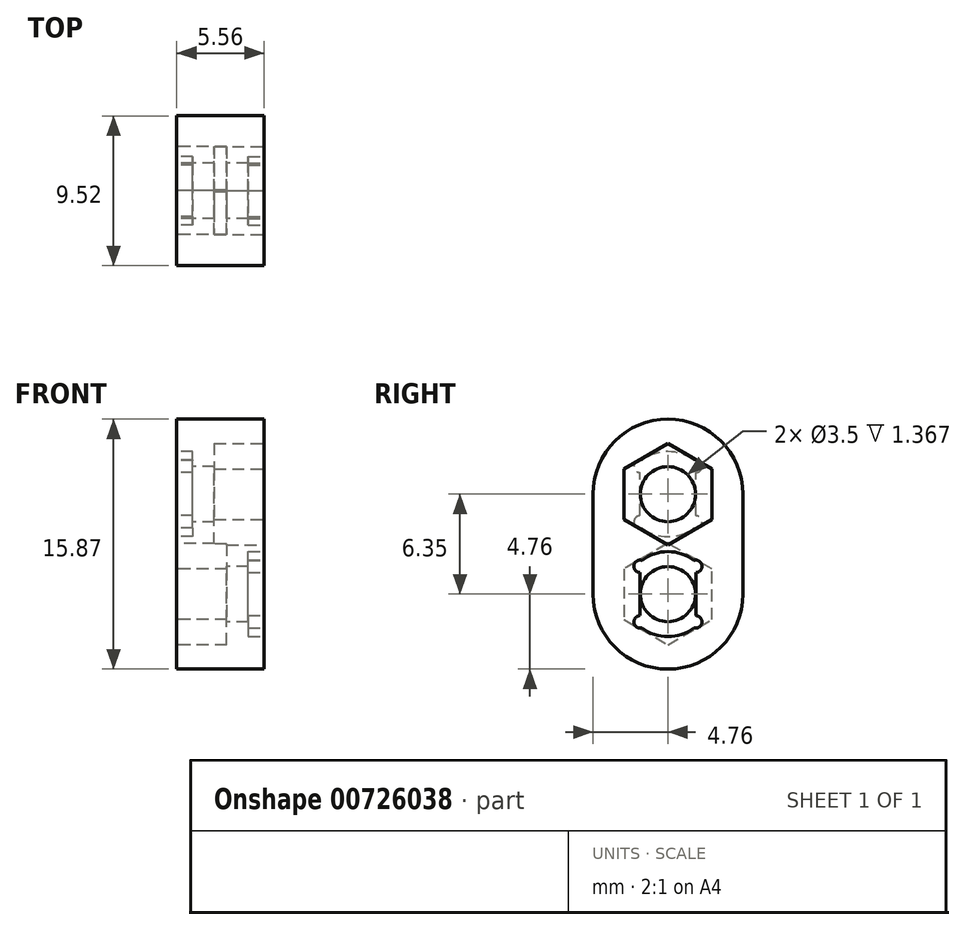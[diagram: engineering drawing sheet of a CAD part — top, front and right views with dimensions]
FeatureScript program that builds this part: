
annotation { "Feature Type Name" : "Feature", "Feature Type Description" : "" }
export const myFeature = defineFeature(function(context is Context, id is Id, definition is map)
    precondition{}
    {
        {
            var Q0;
            Q0=qCreatedBy(makeId("Right.planeOp"),FACE);
            var sketch = newSketch(context, id + "F0", { "sketchPlane" : qUnion([Q0])});
            skCircle(sketch, "E0", {"center": v(0, 0) * mm, "radius": 4.76 * mm});
            skCircle(sketch, "E1", {"center": v(0, 0) * mm, "radius": 1.75 * mm});
            skCircle(sketch, "E2", {"center": v(0, -6.35) * mm, "radius": 4.76 * mm});
            skCircle(sketch, "E3", {"center": v(0, -6.35) * mm, "radius": 1.75 * mm});
            skLineSegment(sketch, "E4", {"start": v(-4.76, 0) * mm, "end": v(-4.76, -6.35) * mm});
            skLineSegment(sketch, "E5", {"start": v(4.76, 0) * mm, "end": v(4.76, -6.35) * mm});
            skSolve(sketch);
        }
        {
            var Q0;
            Q0=makeQuery(id+"F0.imprint","IMPRINT",FACE,{"disambiguationData":[TD([[makeQuery(id+"F0.imprint","IMPRINT",EDGE,{"derivedFrom":sQuery(id+"F0.wireOp",EDGE,"E1")}),-1.0]])]});
            var Q1;
            {var subQ0=sQuery(id+"F0.wireOp",EDGE,"E5");Q1=makeQuery(id+"F0.imprint","IMPRINT",FACE,{"disambiguationData":[TD([[makeQuery(id+"F0.imprint","IMPRINT",EDGE,{"derivedFrom":subQ0}),-1.0]])]});}
            var Q2;
            {var subQ0=sQuery(id+"F0.wireOp",EDGE,"E2");var subQ1=sQuery(id+"F0.wireOp",EDGE,"E0");var subQ2=makeQuery(id+"F0.imprint","INTERSECT",VERTEX,{"disambiguationData":[OD(0.0)],"derivedFrom":[subQ1,subQ0]});Q2=makeQuery(id+"F0.imprint","IMPRINT",FACE,{"disambiguationData":[TD([[makeQuery(id+"F0.imprint","IMPRINT",EDGE,{"disambiguationData":[TD([[subQ2,-1.0]])],"derivedFrom":subQ1}),1.0]])]});}
            var Q3;
            Q3=makeQuery(id+"F0.imprint","IMPRINT",FACE,{"disambiguationData":[TD([[makeQuery(id+"F0.imprint","IMPRINT",EDGE,{"derivedFrom":sQuery(id+"F0.wireOp",EDGE,"E3")}),-1.0]])]});
            var Q4;
            {var subQ0=sQuery(id+"F0.wireOp",EDGE,"E4");Q4=makeQuery(id+"F0.imprint","IMPRINT",FACE,{"disambiguationData":[TD([[makeQuery(id+"F0.imprint","IMPRINT",EDGE,{"derivedFrom":subQ0}),1.0]])]});}
            extrude(context, id + "F1", {"entities" : qUnion([Q0, Q1, Q2, Q3, Q4]), "depth" : 5.56 * mm, "offsetDistance" : 25.4 * mm});
        }
        {
            var Q0;
            Q0=makeQuery(id+"F1.opExtrude","CAP_FACE",FACE,{"disambiguationData":[OSD([sQuery(id+"F0.wireOp",EDGE,"E0"),sQuery(id+"F0.wireOp",EDGE,"E1"),sQuery(id+"F0.wireOp",EDGE,"E2"),sQuery(id+"F0.wireOp",EDGE,"E3"),sQuery(id+"F0.wireOp",EDGE,"E4"),sQuery(id+"F0.wireOp",EDGE,"E5")])],"isStart":false});
            var sketch = newSketch(context, id + "F2", { "sketchPlane" : qUnion([Q0])});
            skLineSegment(sketch, "E6.bottom", {"start": v(-1.77, -8.12) * mm, "end": v(1.77, -8.12) * mm});
            skLineSegment(sketch, "E6.top", {"start": v(-1.77, -4.58) * mm, "end": v(1.77, -4.58) * mm});
            skLineSegment(sketch, "E6.left", {"start": v(-1.77, -8.12) * mm, "end": v(-1.77, -4.58) * mm});
            skLineSegment(sketch, "E6.right", {"start": v(1.77, -8.12) * mm, "end": v(1.77, -4.58) * mm});
            skPoint(sketch, "E6.middle", {"position": v(0, -6.35) * mm});
            skCircle(sketch, "E7", {"center": v(1.77, -4.58) * mm, "radius": 0.4 * mm});
            skCircle(sketch, "E8", {"center": v(-1.77, -4.58) * mm, "radius": 0.4 * mm});
            skCircle(sketch, "E9", {"center": v(-1.77, -8.12) * mm, "radius": 0.4 * mm});
            skCircle(sketch, "E10", {"center": v(1.77, -8.12) * mm, "radius": 0.4 * mm});
            skCircle(sketch, "E11.cCircle", {"center": v(0, 0) * mm, "radius": 3.23 * mm, "construction": true});
            skLineSegment(sketch, "E11.0", {"start": v(0, -3.23) * mm, "end": v(-2.8, -1.61) * mm});
            skLineSegment(sketch, "E11.1", {"start": v(-2.8, -1.61) * mm, "end": v(-2.8, 1.61) * mm});
            skLineSegment(sketch, "E11.2", {"start": v(-2.8, 1.61) * mm, "end": v(0, 3.23) * mm});
            skLineSegment(sketch, "E11.3", {"start": v(0, 3.23) * mm, "end": v(2.8, 1.61) * mm});
            skLineSegment(sketch, "E11.4", {"start": v(2.8, 1.61) * mm, "end": v(2.8, -1.61) * mm});
            skLineSegment(sketch, "E11.5", {"start": v(2.8, -1.61) * mm, "end": v(0, -3.23) * mm});
            skCircle(sketch, "E12", {"center": v(0, -6.35) * mm, "radius": 2.7 * mm});
            skSolve(sketch);
        }
        {
            var Q0;
            {var subQ0=sQuery(id+"F2.wireOp",EDGE,"E6.right");var subQ1=sQuery(id+"F2.wireOp",EDGE,"E6.top");var subQ2=makeQuery(id+"F2.imprint","INTERSECT",VERTEX,{"derivedFrom":[subQ1,subQ0]});Q0=makeQuery(id+"F2.imprint","IMPRINT",FACE,{"disambiguationData":[TD([[makeQuery(id+"F2.imprint","IMPRINT",EDGE,{"disambiguationData":[TD([[subQ2,1.0]])],"derivedFrom":subQ1}),-1.0]])]});}
            var Q1;
            {var subQ0=sQuery(id+"F2.wireOp",EDGE,"E6.right");var subQ1=sQuery(id+"F2.wireOp",EDGE,"E6.top");var subQ2=makeQuery(id+"F2.imprint","INTERSECT",VERTEX,{"derivedFrom":[subQ1,subQ0]});Q1=makeQuery(id+"F2.imprint","IMPRINT",FACE,{"disambiguationData":[TD([[makeQuery(id+"F2.imprint","IMPRINT",EDGE,{"disambiguationData":[TD([[subQ2,1.0]])],"derivedFrom":subQ1}),1.0]])]});}
            var Q2;
            {var subQ0=sQuery(id+"F2.wireOp",EDGE,"E6.right");var subQ1=sQuery(id+"F2.wireOp",EDGE,"E6.bottom");var subQ2=makeQuery(id+"F2.imprint","INTERSECT",VERTEX,{"derivedFrom":[subQ1,subQ0]});Q2=makeQuery(id+"F2.imprint","IMPRINT",FACE,{"disambiguationData":[TD([[makeQuery(id+"F2.imprint","IMPRINT",EDGE,{"disambiguationData":[TD([[subQ2,1.0]])],"derivedFrom":subQ1}),1.0]])]});}
            var Q3;
            {var subQ0=sQuery(id+"F2.wireOp",EDGE,"E6.right");var subQ1=sQuery(id+"F2.wireOp",EDGE,"E6.bottom");var subQ2=makeQuery(id+"F2.imprint","INTERSECT",VERTEX,{"derivedFrom":[subQ1,subQ0]});Q3=makeQuery(id+"F2.imprint","IMPRINT",FACE,{"disambiguationData":[TD([[makeQuery(id+"F2.imprint","IMPRINT",EDGE,{"disambiguationData":[TD([[subQ2,1.0]])],"derivedFrom":subQ1}),-1.0]])]});}
            var Q4;
            {var subQ0=sQuery(id+"F2.wireOp",EDGE,"E6.left");var subQ1=sQuery(id+"F2.wireOp",EDGE,"E6.bottom");var subQ2=makeQuery(id+"F2.imprint","INTERSECT",VERTEX,{"derivedFrom":[subQ1,subQ0]});Q4=makeQuery(id+"F2.imprint","IMPRINT",FACE,{"disambiguationData":[TD([[makeQuery(id+"F2.imprint","IMPRINT",EDGE,{"disambiguationData":[TD([[subQ2,-1.0]])],"derivedFrom":subQ1}),-1.0]])]});}
            var Q5;
            {var subQ0=sQuery(id+"F2.wireOp",EDGE,"E6.left");var subQ1=sQuery(id+"F2.wireOp",EDGE,"E6.bottom");var subQ2=makeQuery(id+"F2.imprint","INTERSECT",VERTEX,{"derivedFrom":[subQ1,subQ0]});Q5=makeQuery(id+"F2.imprint","IMPRINT",FACE,{"disambiguationData":[TD([[makeQuery(id+"F2.imprint","IMPRINT",EDGE,{"disambiguationData":[TD([[subQ2,-1.0]])],"derivedFrom":subQ1}),1.0]])]});}
            var Q6;
            {var subQ0=sQuery(id+"F2.wireOp",EDGE,"E6.left");var subQ1=sQuery(id+"F2.wireOp",EDGE,"E6.top");var subQ2=makeQuery(id+"F2.imprint","INTERSECT",VERTEX,{"derivedFrom":[subQ1,subQ0]});Q6=makeQuery(id+"F2.imprint","IMPRINT",FACE,{"disambiguationData":[TD([[makeQuery(id+"F2.imprint","IMPRINT",EDGE,{"disambiguationData":[TD([[subQ2,-1.0]])],"derivedFrom":subQ1}),-1.0]])]});}
            var Q7;
            {var subQ0=sQuery(id+"F2.wireOp",EDGE,"E6.left");var subQ1=makeQuery(id+"F1.opExtrude","CAP_EDGE",EDGE,{"disambiguationData":[OSD([sQuery(id+"F0.wireOp",EDGE,"E3")])],"isStart":false});var subQ2=makeQuery(id+"F2.imprint","INTERSECT",VERTEX,{"disambiguationData":[OD(0.0)],"derivedFrom":[subQ1,subQ0]});Q7=makeQuery(id+"F2.imprint","IMPRINT",FACE,{"disambiguationData":[TD([[makeQuery(id+"F2.imprint","IMPRINT",EDGE,{"disambiguationData":[TD([[subQ2,-1.0]])],"derivedFrom":subQ0}),-1.0]])]});}
            var Q8;
            {var subQ0=sQuery(id+"F2.wireOp",EDGE,"E6.left");var subQ1=sQuery(id+"F2.wireOp",EDGE,"E6.top");var subQ2=makeQuery(id+"F2.imprint","INTERSECT",VERTEX,{"derivedFrom":[subQ1,subQ0]});Q8=makeQuery(id+"F2.imprint","IMPRINT",FACE,{"disambiguationData":[TD([[makeQuery(id+"F2.imprint","IMPRINT",EDGE,{"disambiguationData":[TD([[subQ2,-1.0]])],"derivedFrom":subQ1}),1.0]])]});}
            var Q9;
            {var subQ1=sQuery(id+"F2.wireOp",EDGE,"E6.top");var subQ7=sQuery(id+"F2.wireOp",EDGE,"E8");var subQ11=makeQuery(id+"F2.imprint","INTERSECT",VERTEX,{"derivedFrom":[subQ1,subQ7]});Q9=makeQuery(id+"F2.imprint","IMPRINT",FACE,{"disambiguationData":[TD([[makeQuery(id+"F2.imprint","IMPRINT",EDGE,{"disambiguationData":[TD([[subQ11,-1.0]])],"derivedFrom":subQ1}),-1.0]])]});}
            var Q10;
            {var subQ0=sQuery(id+"F2.wireOp",EDGE,"E9");var subQ1=sQuery(id+"F2.wireOp",EDGE,"E6.bottom");var subQ2=makeQuery(id+"F2.imprint","INTERSECT",VERTEX,{"derivedFrom":[subQ1,subQ0]});Q10=makeQuery(id+"F2.imprint","IMPRINT",FACE,{"disambiguationData":[TD([[makeQuery(id+"F2.imprint","IMPRINT",EDGE,{"disambiguationData":[TD([[subQ2,-1.0]])],"derivedFrom":subQ1}),1.0]])]});}
            var Q11;
            {var subQ0=sQuery(id+"F2.wireOp",EDGE,"E12");var subQ1=sQuery(id+"F2.wireOp",EDGE,"E6.top");var subQ10=makeQuery(id+"F2.imprint","INTERSECT",VERTEX,{"disambiguationData":[OD(0.0)],"derivedFrom":[subQ1,subQ0]});Q11=makeQuery(id+"F2.imprint","IMPRINT",FACE,{"disambiguationData":[TD([[makeQuery(id+"F2.imprint","IMPRINT",EDGE,{"disambiguationData":[TD([[subQ10,-1.0]])],"derivedFrom":subQ1}),-1.0]])]});}
            var Q12;
            {var subQ0=sQuery(id+"F2.wireOp",EDGE,"E12");var subQ1=sQuery(id+"F2.wireOp",EDGE,"E6.top");var subQ2=makeQuery(id+"F2.imprint","INTERSECT",VERTEX,{"disambiguationData":[OD(1.0)],"derivedFrom":[subQ1,subQ0]});Q12=makeQuery(id+"F2.imprint","IMPRINT",FACE,{"disambiguationData":[TD([[makeQuery(id+"F2.imprint","IMPRINT",EDGE,{"disambiguationData":[TD([[subQ2,-1.0]])],"derivedFrom":subQ1}),-1.0]])]});}
            var Q13;
            {var subQ0=sQuery(id+"F2.wireOp",EDGE,"E12");var subQ1=sQuery(id+"F2.wireOp",EDGE,"E6.top");var subQ2=makeQuery(id+"F2.imprint","INTERSECT",VERTEX,{"disambiguationData":[OD(0.0)],"derivedFrom":[subQ1,subQ0]});Q13=makeQuery(id+"F2.imprint","IMPRINT",FACE,{"disambiguationData":[TD([[makeQuery(id+"F2.imprint","IMPRINT",EDGE,{"disambiguationData":[TD([[subQ2,-1.0]])],"derivedFrom":subQ1}),1.0]])]});}
            var Q14;
            {var subQ0=sQuery(id+"F2.wireOp",EDGE,"E12");var subQ7=sQuery(id+"F2.wireOp",EDGE,"E6.bottom");var subQ8=makeQuery(id+"F2.imprint","INTERSECT",VERTEX,{"disambiguationData":[OD(0.0)],"derivedFrom":[subQ7,subQ0]});Q14=makeQuery(id+"F2.imprint","IMPRINT",FACE,{"disambiguationData":[TD([[makeQuery(id+"F2.imprint","IMPRINT",EDGE,{"disambiguationData":[TD([[subQ8,-1.0]])],"derivedFrom":subQ7}),1.0]])]});}
            var Q15;
            {var subQ0=sQuery(id+"F2.wireOp",EDGE,"E12");var subQ1=sQuery(id+"F2.wireOp",EDGE,"E6.bottom");var subQ2=makeQuery(id+"F2.imprint","INTERSECT",VERTEX,{"disambiguationData":[OD(1.0)],"derivedFrom":[subQ1,subQ0]});Q15=makeQuery(id+"F2.imprint","IMPRINT",FACE,{"disambiguationData":[TD([[makeQuery(id+"F2.imprint","IMPRINT",EDGE,{"disambiguationData":[TD([[subQ2,-1.0]])],"derivedFrom":subQ1}),1.0]])]});}
            var Q16;
            {var subQ0=sQuery(id+"F2.wireOp",EDGE,"E12");var subQ1=sQuery(id+"F2.wireOp",EDGE,"E6.bottom");var subQ2=makeQuery(id+"F2.imprint","INTERSECT",VERTEX,{"disambiguationData":[OD(0.0)],"derivedFrom":[subQ1,subQ0]});Q16=makeQuery(id+"F2.imprint","IMPRINT",FACE,{"disambiguationData":[TD([[makeQuery(id+"F2.imprint","IMPRINT",EDGE,{"disambiguationData":[TD([[subQ2,-1.0]])],"derivedFrom":subQ1}),-1.0]])]});}
            var Q17;
            {var subQ0=sQuery(id+"F2.wireOp",EDGE,"E12");var subQ1=sQuery(id+"F2.wireOp",EDGE,"E8");var subQ2=makeQuery(id+"F2.imprint","INTERSECT",VERTEX,{"disambiguationData":[OD(0.0)],"derivedFrom":[subQ1,subQ0]});Q17=makeQuery(id+"F2.imprint","IMPRINT",FACE,{"disambiguationData":[TD([[makeQuery(id+"F2.imprint","IMPRINT",EDGE,{"disambiguationData":[TD([[subQ2,-1.0]])],"derivedFrom":subQ1}),1.0]])]});}
            var Q18;
            {var subQ0=sQuery(id+"F2.wireOp",EDGE,"E12");var subQ1=sQuery(id+"F2.wireOp",EDGE,"E7");var subQ2=makeQuery(id+"F2.imprint","INTERSECT",VERTEX,{"disambiguationData":[OD(0.0)],"derivedFrom":[subQ1,subQ0]});Q18=makeQuery(id+"F2.imprint","IMPRINT",FACE,{"disambiguationData":[TD([[makeQuery(id+"F2.imprint","IMPRINT",EDGE,{"disambiguationData":[TD([[subQ2,1.0]])],"derivedFrom":subQ1}),1.0]])]});}
            var Q19;
            {var subQ0=sQuery(id+"F2.wireOp",EDGE,"E12");var subQ1=sQuery(id+"F2.wireOp",EDGE,"E10");var subQ2=makeQuery(id+"F2.imprint","INTERSECT",VERTEX,{"disambiguationData":[OD(0.0)],"derivedFrom":[subQ1,subQ0]});Q19=makeQuery(id+"F2.imprint","IMPRINT",FACE,{"disambiguationData":[TD([[makeQuery(id+"F2.imprint","IMPRINT",EDGE,{"disambiguationData":[TD([[subQ2,1.0]])],"derivedFrom":subQ1}),1.0]])]});}
            var Q20;
            {var subQ0=sQuery(id+"F2.wireOp",EDGE,"E12");var subQ1=sQuery(id+"F2.wireOp",EDGE,"E9");var subQ2=makeQuery(id+"F2.imprint","INTERSECT",VERTEX,{"disambiguationData":[OD(0.0)],"derivedFrom":[subQ1,subQ0]});Q20=makeQuery(id+"F2.imprint","IMPRINT",FACE,{"disambiguationData":[TD([[makeQuery(id+"F2.imprint","IMPRINT",EDGE,{"disambiguationData":[TD([[subQ2,-1.0]])],"derivedFrom":subQ1}),1.0]])]});}
            var Q21;
            {var subQ0=sQuery(id+"F2.wireOp",EDGE,"E8");var subQ1=sQuery(id+"F2.wireOp",EDGE,"E6.top");var subQ2=makeQuery(id+"F2.imprint","INTERSECT",VERTEX,{"derivedFrom":[subQ1,subQ0]});Q21=makeQuery(id+"F2.imprint","IMPRINT",FACE,{"disambiguationData":[TD([[makeQuery(id+"F2.imprint","IMPRINT",EDGE,{"disambiguationData":[TD([[subQ2,-1.0]])],"derivedFrom":subQ1}),1.0]])]});}
            var Q22;
            {var subQ0=sQuery(id+"F2.wireOp",EDGE,"E9");var subQ1=sQuery(id+"F2.wireOp",EDGE,"E6.bottom");var subQ2=makeQuery(id+"F2.imprint","INTERSECT",VERTEX,{"derivedFrom":[subQ1,subQ0]});Q22=makeQuery(id+"F2.imprint","IMPRINT",FACE,{"disambiguationData":[TD([[makeQuery(id+"F2.imprint","IMPRINT",EDGE,{"disambiguationData":[TD([[subQ2,-1.0]])],"derivedFrom":subQ1}),-1.0]])]});}
            extrude(context, id + "F3", {"entities" : qUnion([Q0, Q1, Q2, Q3, Q4, Q5, Q6, Q7, Q8, Q9, Q10, Q11, Q12, Q13, Q14, Q15, Q16, Q17, Q18, Q19, Q20, Q21, Q22]), "operationType" : NewBodyOperationType.REMOVE, "oppositeDirection" : true, "depth" : 1.02 * mm, "offsetDistance" : 25.4 * mm});
        }
        {
            var Q0;
            Q0=makeQuery(id+"F1.opExtrude","CAP_FACE",FACE,{"disambiguationData":[OSD([sQuery(id+"F0.wireOp",EDGE,"E0"),sQuery(id+"F0.wireOp",EDGE,"E1"),sQuery(id+"F0.wireOp",EDGE,"E2"),sQuery(id+"F0.wireOp",EDGE,"E3"),sQuery(id+"F0.wireOp",EDGE,"E4"),sQuery(id+"F0.wireOp",EDGE,"E5")])],"isStart":true});
            var sketch = newSketch(context, id + "F4", { "sketchPlane" : qUnion([Q0])});
            skLineSegment(sketch, "E13.bottom", {"start": v(-1.77, -1.77) * mm, "end": v(1.77, -1.77) * mm});
            skLineSegment(sketch, "E13.top", {"start": v(-1.77, 1.77) * mm, "end": v(1.77, 1.77) * mm});
            skLineSegment(sketch, "E13.left", {"start": v(-1.77, -1.77) * mm, "end": v(-1.77, 1.77) * mm});
            skLineSegment(sketch, "E13.right", {"start": v(1.77, -1.77) * mm, "end": v(1.77, 1.77) * mm});
            skPoint(sketch, "E13.middle", {"position": v(0, 0) * mm});
            skCircle(sketch, "E14", {"center": v(1.77, 1.77) * mm, "radius": 0.4 * mm});
            skCircle(sketch, "E15", {"center": v(-1.77, 1.77) * mm, "radius": 0.4 * mm});
            skCircle(sketch, "E16", {"center": v(-1.77, -1.77) * mm, "radius": 0.4 * mm});
            skCircle(sketch, "E17", {"center": v(1.77, -1.77) * mm, "radius": 0.4 * mm});
            skCircle(sketch, "E18.cCircle", {"center": v(0, -6.35) * mm, "radius": 3.23 * mm, "construction": true});
            skLineSegment(sketch, "E18.0", {"start": v(0, -9.58) * mm, "end": v(-2.8, -7.96) * mm});
            skLineSegment(sketch, "E18.1", {"start": v(-2.8, -7.96) * mm, "end": v(-2.8, -4.74) * mm});
            skLineSegment(sketch, "E18.2", {"start": v(-2.8, -4.74) * mm, "end": v(0, -3.12) * mm});
            skLineSegment(sketch, "E18.3", {"start": v(0, -3.12) * mm, "end": v(2.8, -4.74) * mm});
            skLineSegment(sketch, "E18.4", {"start": v(2.8, -4.74) * mm, "end": v(2.8, -7.96) * mm});
            skLineSegment(sketch, "E18.5", {"start": v(2.8, -7.96) * mm, "end": v(0, -9.58) * mm});
            skCircle(sketch, "E19", {"center": v(0, 0) * mm, "radius": 2.7 * mm});
            skSolve(sketch);
        }
        {
            var Q0;
            {var subQ0=sQuery(id+"F4.wireOp",EDGE,"E13.right");var subQ1=sQuery(id+"F4.wireOp",EDGE,"E13.bottom");var subQ2=makeQuery(id+"F4.imprint","INTERSECT",VERTEX,{"derivedFrom":[subQ1,subQ0]});Q0=makeQuery(id+"F4.imprint","IMPRINT",FACE,{"disambiguationData":[TD([[makeQuery(id+"F4.imprint","IMPRINT",EDGE,{"disambiguationData":[TD([[subQ2,1.0]])],"derivedFrom":subQ1}),1.0]])]});}
            var Q1;
            {var subQ0=sQuery(id+"F4.wireOp",EDGE,"E13.right");var subQ1=sQuery(id+"F4.wireOp",EDGE,"E13.bottom");var subQ2=makeQuery(id+"F4.imprint","INTERSECT",VERTEX,{"derivedFrom":[subQ1,subQ0]});Q1=makeQuery(id+"F4.imprint","IMPRINT",FACE,{"disambiguationData":[TD([[makeQuery(id+"F4.imprint","IMPRINT",EDGE,{"disambiguationData":[TD([[subQ2,1.0]])],"derivedFrom":subQ1}),-1.0]])]});}
            var Q2;
            {var subQ0=sQuery(id+"F4.wireOp",EDGE,"E13.left");var subQ1=sQuery(id+"F4.wireOp",EDGE,"E13.bottom");var subQ2=makeQuery(id+"F4.imprint","INTERSECT",VERTEX,{"derivedFrom":[subQ1,subQ0]});Q2=makeQuery(id+"F4.imprint","IMPRINT",FACE,{"disambiguationData":[TD([[makeQuery(id+"F4.imprint","IMPRINT",EDGE,{"disambiguationData":[TD([[subQ2,-1.0]])],"derivedFrom":subQ1}),1.0]])]});}
            var Q3;
            {var subQ0=sQuery(id+"F4.wireOp",EDGE,"E13.left");var subQ1=sQuery(id+"F4.wireOp",EDGE,"E13.bottom");var subQ2=makeQuery(id+"F4.imprint","INTERSECT",VERTEX,{"derivedFrom":[subQ1,subQ0]});Q3=makeQuery(id+"F4.imprint","IMPRINT",FACE,{"disambiguationData":[TD([[makeQuery(id+"F4.imprint","IMPRINT",EDGE,{"disambiguationData":[TD([[subQ2,-1.0]])],"derivedFrom":subQ1}),-1.0]])]});}
            var Q4;
            {var subQ0=sQuery(id+"F4.wireOp",EDGE,"E13.left");var subQ1=sQuery(id+"F4.wireOp",EDGE,"E13.top");var subQ2=makeQuery(id+"F4.imprint","INTERSECT",VERTEX,{"derivedFrom":[subQ1,subQ0]});Q4=makeQuery(id+"F4.imprint","IMPRINT",FACE,{"disambiguationData":[TD([[makeQuery(id+"F4.imprint","IMPRINT",EDGE,{"disambiguationData":[TD([[subQ2,-1.0]])],"derivedFrom":subQ1}),-1.0]])]});}
            var Q5;
            {var subQ0=sQuery(id+"F4.wireOp",EDGE,"E13.left");var subQ1=sQuery(id+"F4.wireOp",EDGE,"E13.top");var subQ2=makeQuery(id+"F4.imprint","INTERSECT",VERTEX,{"derivedFrom":[subQ1,subQ0]});Q5=makeQuery(id+"F4.imprint","IMPRINT",FACE,{"disambiguationData":[TD([[makeQuery(id+"F4.imprint","IMPRINT",EDGE,{"disambiguationData":[TD([[subQ2,-1.0]])],"derivedFrom":subQ1}),1.0]])]});}
            var Q6;
            {var subQ0=sQuery(id+"F4.wireOp",EDGE,"E13.right");var subQ1=sQuery(id+"F4.wireOp",EDGE,"E13.top");var subQ2=makeQuery(id+"F4.imprint","INTERSECT",VERTEX,{"derivedFrom":[subQ1,subQ0]});Q6=makeQuery(id+"F4.imprint","IMPRINT",FACE,{"disambiguationData":[TD([[makeQuery(id+"F4.imprint","IMPRINT",EDGE,{"disambiguationData":[TD([[subQ2,1.0]])],"derivedFrom":subQ1}),-1.0]])]});}
            var Q7;
            {var subQ0=sQuery(id+"F4.wireOp",EDGE,"E13.right");var subQ1=sQuery(id+"F4.wireOp",EDGE,"E13.top");var subQ2=makeQuery(id+"F4.imprint","INTERSECT",VERTEX,{"derivedFrom":[subQ1,subQ0]});Q7=makeQuery(id+"F4.imprint","IMPRINT",FACE,{"disambiguationData":[TD([[makeQuery(id+"F4.imprint","IMPRINT",EDGE,{"disambiguationData":[TD([[subQ2,1.0]])],"derivedFrom":subQ1}),1.0]])]});}
            var Q8;
            {var subQ1=sQuery(id+"F4.wireOp",EDGE,"E13.top");var subQ7=sQuery(id+"F4.wireOp",EDGE,"E15");var subQ11=makeQuery(id+"F4.imprint","INTERSECT",VERTEX,{"derivedFrom":[subQ1,subQ7]});Q8=makeQuery(id+"F4.imprint","IMPRINT",FACE,{"disambiguationData":[TD([[makeQuery(id+"F4.imprint","IMPRINT",EDGE,{"disambiguationData":[TD([[subQ11,-1.0]])],"derivedFrom":subQ1}),-1.0]])]});}
            var Q9;
            {var subQ0=sQuery(id+"F4.wireOp",EDGE,"E19");var subQ1=sQuery(id+"F4.wireOp",EDGE,"E13.top");var subQ10=makeQuery(id+"F4.imprint","INTERSECT",VERTEX,{"disambiguationData":[OD(0.0)],"derivedFrom":[subQ1,subQ0]});Q9=makeQuery(id+"F4.imprint","IMPRINT",FACE,{"disambiguationData":[TD([[makeQuery(id+"F4.imprint","IMPRINT",EDGE,{"disambiguationData":[TD([[subQ10,-1.0]])],"derivedFrom":subQ1}),-1.0]])]});}
            var Q10;
            {var subQ0=sQuery(id+"F4.wireOp",EDGE,"E19");var subQ7=sQuery(id+"F4.wireOp",EDGE,"E13.bottom");var subQ8=makeQuery(id+"F4.imprint","INTERSECT",VERTEX,{"disambiguationData":[OD(0.0)],"derivedFrom":[subQ7,subQ0]});Q10=makeQuery(id+"F4.imprint","IMPRINT",FACE,{"disambiguationData":[TD([[makeQuery(id+"F4.imprint","IMPRINT",EDGE,{"disambiguationData":[TD([[subQ8,-1.0]])],"derivedFrom":subQ7}),1.0]])]});}
            var Q11;
            {var subQ0=sQuery(id+"F4.wireOp",EDGE,"E16");var subQ1=sQuery(id+"F4.wireOp",EDGE,"E13.bottom");var subQ2=makeQuery(id+"F4.imprint","INTERSECT",VERTEX,{"derivedFrom":[subQ1,subQ0]});Q11=makeQuery(id+"F4.imprint","IMPRINT",FACE,{"disambiguationData":[TD([[makeQuery(id+"F4.imprint","IMPRINT",EDGE,{"disambiguationData":[TD([[subQ2,-1.0]])],"derivedFrom":subQ1}),1.0]])]});}
            var Q12;
            {var subQ0=sQuery(id+"F4.wireOp",EDGE,"E19");var subQ1=sQuery(id+"F4.wireOp",EDGE,"E13.bottom");var subQ2=makeQuery(id+"F4.imprint","INTERSECT",VERTEX,{"disambiguationData":[OD(1.0)],"derivedFrom":[subQ1,subQ0]});Q12=makeQuery(id+"F4.imprint","IMPRINT",FACE,{"disambiguationData":[TD([[makeQuery(id+"F4.imprint","IMPRINT",EDGE,{"disambiguationData":[TD([[subQ2,-1.0]])],"derivedFrom":subQ1}),1.0]])]});}
            var Q13;
            {var subQ0=sQuery(id+"F4.wireOp",EDGE,"E19");var subQ1=sQuery(id+"F4.wireOp",EDGE,"E13.top");var subQ2=makeQuery(id+"F4.imprint","INTERSECT",VERTEX,{"disambiguationData":[OD(1.0)],"derivedFrom":[subQ1,subQ0]});Q13=makeQuery(id+"F4.imprint","IMPRINT",FACE,{"disambiguationData":[TD([[makeQuery(id+"F4.imprint","IMPRINT",EDGE,{"disambiguationData":[TD([[subQ2,-1.0]])],"derivedFrom":subQ1}),-1.0]])]});}
            var Q14;
            {var subQ0=sQuery(id+"F4.wireOp",EDGE,"E19");var subQ1=sQuery(id+"F4.wireOp",EDGE,"E13.top");var subQ2=makeQuery(id+"F4.imprint","INTERSECT",VERTEX,{"disambiguationData":[OD(0.0)],"derivedFrom":[subQ1,subQ0]});Q14=makeQuery(id+"F4.imprint","IMPRINT",FACE,{"disambiguationData":[TD([[makeQuery(id+"F4.imprint","IMPRINT",EDGE,{"disambiguationData":[TD([[subQ2,-1.0]])],"derivedFrom":subQ1}),1.0]])]});}
            var Q15;
            {var subQ0=sQuery(id+"F4.wireOp",EDGE,"E19");var subQ1=sQuery(id+"F4.wireOp",EDGE,"E13.bottom");var subQ2=makeQuery(id+"F4.imprint","INTERSECT",VERTEX,{"disambiguationData":[OD(0.0)],"derivedFrom":[subQ1,subQ0]});Q15=makeQuery(id+"F4.imprint","IMPRINT",FACE,{"disambiguationData":[TD([[makeQuery(id+"F4.imprint","IMPRINT",EDGE,{"disambiguationData":[TD([[subQ2,-1.0]])],"derivedFrom":subQ1}),-1.0]])]});}
            var Q16;
            {var subQ0=sQuery(id+"F4.wireOp",EDGE,"E19");var subQ1=sQuery(id+"F4.wireOp",EDGE,"E15");var subQ2=makeQuery(id+"F4.imprint","INTERSECT",VERTEX,{"disambiguationData":[OD(0.0)],"derivedFrom":[subQ1,subQ0]});Q16=makeQuery(id+"F4.imprint","IMPRINT",FACE,{"disambiguationData":[TD([[makeQuery(id+"F4.imprint","IMPRINT",EDGE,{"disambiguationData":[TD([[subQ2,-1.0]])],"derivedFrom":subQ1}),1.0]])]});}
            var Q17;
            {var subQ0=sQuery(id+"F4.wireOp",EDGE,"E19");var subQ1=sQuery(id+"F4.wireOp",EDGE,"E14");var subQ2=makeQuery(id+"F4.imprint","INTERSECT",VERTEX,{"disambiguationData":[OD(0.0)],"derivedFrom":[subQ1,subQ0]});Q17=makeQuery(id+"F4.imprint","IMPRINT",FACE,{"disambiguationData":[TD([[makeQuery(id+"F4.imprint","IMPRINT",EDGE,{"disambiguationData":[TD([[subQ2,1.0]])],"derivedFrom":subQ1}),1.0]])]});}
            var Q18;
            {var subQ0=sQuery(id+"F4.wireOp",EDGE,"E19");var subQ1=sQuery(id+"F4.wireOp",EDGE,"E17");var subQ2=makeQuery(id+"F4.imprint","INTERSECT",VERTEX,{"disambiguationData":[OD(0.0)],"derivedFrom":[subQ1,subQ0]});Q18=makeQuery(id+"F4.imprint","IMPRINT",FACE,{"disambiguationData":[TD([[makeQuery(id+"F4.imprint","IMPRINT",EDGE,{"disambiguationData":[TD([[subQ2,1.0]])],"derivedFrom":subQ1}),1.0]])]});}
            var Q19;
            {var subQ0=sQuery(id+"F4.wireOp",EDGE,"E19");var subQ1=sQuery(id+"F4.wireOp",EDGE,"E16");var subQ2=makeQuery(id+"F4.imprint","INTERSECT",VERTEX,{"disambiguationData":[OD(0.0)],"derivedFrom":[subQ1,subQ0]});Q19=makeQuery(id+"F4.imprint","IMPRINT",FACE,{"disambiguationData":[TD([[makeQuery(id+"F4.imprint","IMPRINT",EDGE,{"disambiguationData":[TD([[subQ2,-1.0]])],"derivedFrom":subQ1}),1.0]])]});}
            var Q20;
            {var subQ0=sQuery(id+"F4.wireOp",EDGE,"E15");var subQ1=sQuery(id+"F4.wireOp",EDGE,"E13.top");var subQ2=makeQuery(id+"F4.imprint","INTERSECT",VERTEX,{"derivedFrom":[subQ1,subQ0]});Q20=makeQuery(id+"F4.imprint","IMPRINT",FACE,{"disambiguationData":[TD([[makeQuery(id+"F4.imprint","IMPRINT",EDGE,{"disambiguationData":[TD([[subQ2,-1.0]])],"derivedFrom":subQ1}),1.0]])]});}
            var Q21;
            {var subQ0=sQuery(id+"F4.wireOp",EDGE,"E16");var subQ1=sQuery(id+"F4.wireOp",EDGE,"E13.bottom");var subQ2=makeQuery(id+"F4.imprint","INTERSECT",VERTEX,{"derivedFrom":[subQ1,subQ0]});Q21=makeQuery(id+"F4.imprint","IMPRINT",FACE,{"disambiguationData":[TD([[makeQuery(id+"F4.imprint","IMPRINT",EDGE,{"disambiguationData":[TD([[subQ2,-1.0]])],"derivedFrom":subQ1}),-1.0]])]});}
            extrude(context, id + "F5", {"entities" : qUnion([Q0, Q1, Q2, Q3, Q4, Q5, Q6, Q7, Q8, Q9, Q10, Q11, Q12, Q13, Q14, Q15, Q16, Q17, Q18, Q19, Q20, Q21]), "operationType" : NewBodyOperationType.REMOVE, "oppositeDirection" : true, "depth" : 1.02 * mm, "offsetDistance" : 25.4 * mm});
        }
        {
            var Q0;
            Q0=makeQuery(id+"F2.imprint","IMPRINT",FACE,{"disambiguationData":[TD([[makeQuery(id+"F2.imprint","IMPRINT",EDGE,{"derivedFrom":sQuery(id+"F2.wireOp",EDGE,"E11.0")}),-1.0]])]});
            extrude(context, id + "F6", {"entities" : qUnion([Q0]), "operationType" : NewBodyOperationType.REMOVE, "oppositeDirection" : true, "depth" : 3.17 * mm, "offsetDistance" : 25.4 * mm});
        }
        {
            var Q0;
            Q0=makeQuery(id+"F4.imprint","IMPRINT",FACE,{"disambiguationData":[TD([[makeQuery(id+"F4.imprint","IMPRINT",EDGE,{"derivedFrom":sQuery(id+"F4.wireOp",EDGE,"E18.0")}),-1.0]])]});
            extrude(context, id + "F7", {"entities" : qUnion([Q0]), "operationType" : NewBodyOperationType.REMOVE, "oppositeDirection" : true, "depth" : 3.17 * mm, "offsetDistance" : 25.4 * mm});
        }
    });
